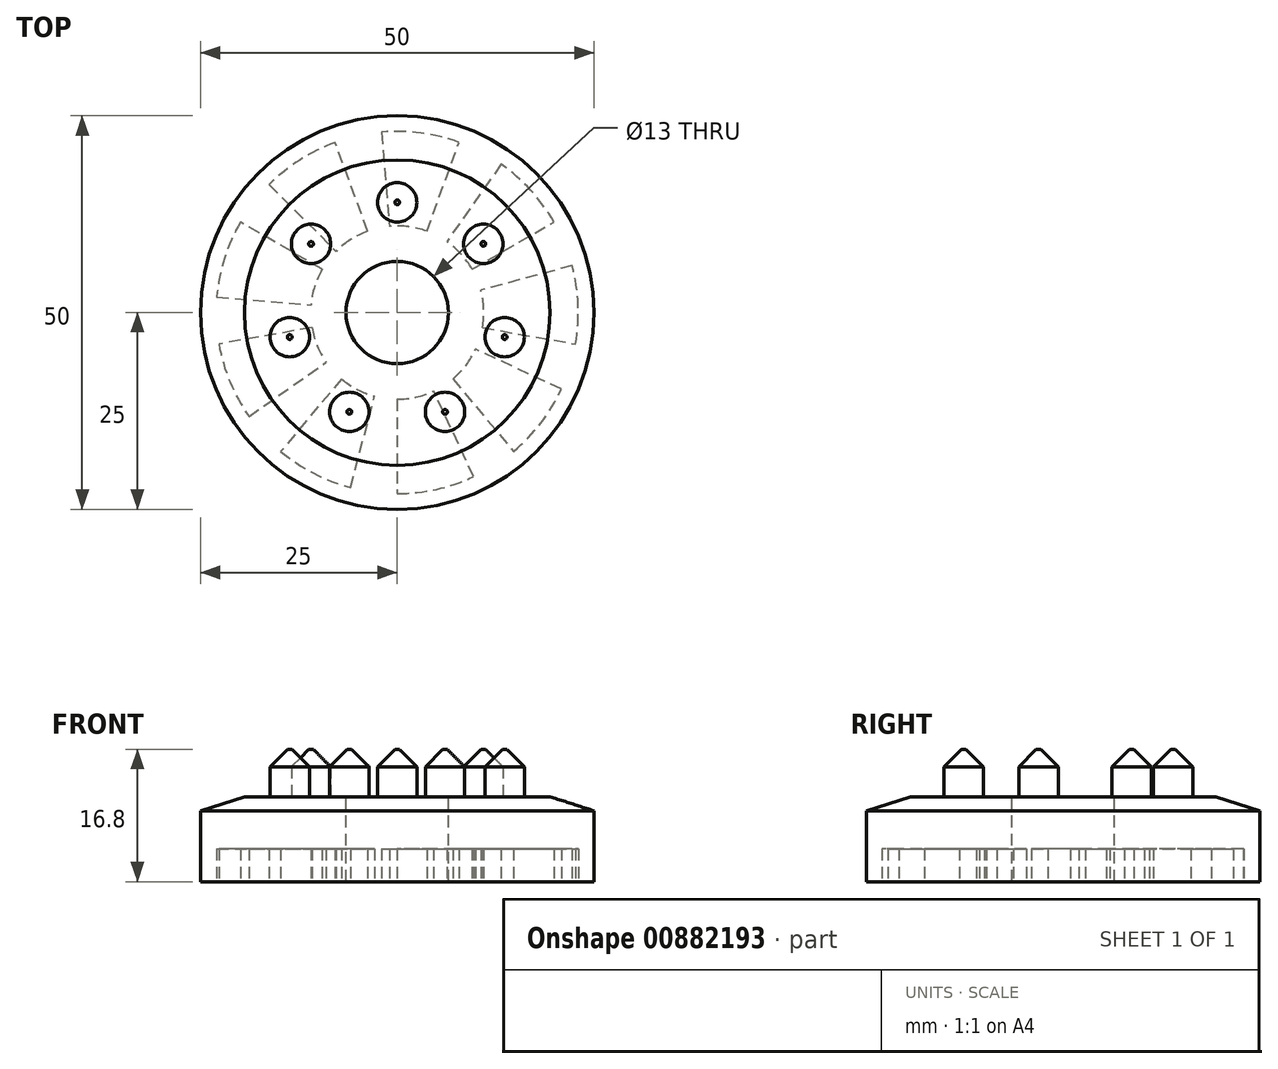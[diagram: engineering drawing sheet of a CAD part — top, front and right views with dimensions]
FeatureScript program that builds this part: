
annotation { "Feature Type Name" : "Feature", "Feature Type Description" : "" }
export const myFeature = defineFeature(function(context is Context, id is Id, definition is map)
    precondition{}
    {
        {
            var Q0;
            Q0=qCreatedBy(makeId("Top.planeOp"),FACE);
            var sketch = newSketch(context, id + "F0", { "sketchPlane" : qUnion([Q0])});
            skCircle(sketch, "E0", {"center": v(0, 0) * mm, "radius": 25 * mm});
            skSolve(sketch);
        }
        {
            var Q0;
            Q0 = qSketchRegion(id + "F0", true);
            extrude(context, id + "F1", {"entities" : qUnion([Q0]), "depth" : 10.8 * mm, "offsetDistance" : 25 * mm});
        }
        {
            var Q0;
            Q0=makeQuery(id+"F1.opExtrude","CAP_EDGE",EDGE,{"disambiguationData":[OSD([sQuery(id+"F0.wireOp",EDGE,"E0")])],"isStart":false});
            chamfer(context, id + "F2", {"entities" : qUnion([Q0]), "chamferType" : ChamferType.TWO_OFFSETS, "width1" : 5.6 * mm, "oppositeDirection" : false, "width2" : 1.8 * mm, "tangentPropagation" : true});
        }
        {
            var Q0;
            Q0=makeQuery(id+"F1.opExtrude","CAP_FACE",FACE,{"disambiguationData":[OSD([sQuery(id+"F0.wireOp",EDGE,"E0")])],"isStart":false});
            var sketch = newSketch(context, id + "F3", { "sketchPlane" : qUnion([Q0])});
            skCircle(sketch, "E1", {"center": v(0, 0) * mm, "radius": 6.5 * mm});
            skCircle(sketch, "E2", {"center": v(0, 14) * mm, "radius": 2.5 * mm});
            skCircle(sketch, "E3.1.0", {"center": v(-10.95, 8.73) * mm, "radius": 2.5 * mm});
            skCircle(sketch, "E3.2.0", {"center": v(-13.65, -3.12) * mm, "radius": 2.5 * mm});
            skCircle(sketch, "E3.3.0", {"center": v(-6.07, -12.61) * mm, "radius": 2.5 * mm});
            skCircle(sketch, "E3.4.0", {"center": v(6.07, -12.61) * mm, "radius": 2.5 * mm});
            skCircle(sketch, "E3.5.0", {"center": v(13.65, -3.12) * mm, "radius": 2.5 * mm});
            skCircle(sketch, "E3.6.0", {"center": v(10.95, 8.73) * mm, "radius": 2.5 * mm});
            skSolve(sketch);
        }
        {
            var Q0;
            Q0=makeQuery(id+"F3.imprint","IMPRINT",FACE,{"disambiguationData":[TD([[makeQuery(id+"F3.imprint","IMPRINT",EDGE,{"derivedFrom":sQuery(id+"F3.wireOp",EDGE,"E3.1.0")}),1.0]])]});
            var Q1;
            Q1=makeQuery(id+"F3.imprint","IMPRINT",FACE,{"disambiguationData":[TD([[makeQuery(id+"F3.imprint","IMPRINT",EDGE,{"derivedFrom":sQuery(id+"F3.wireOp",EDGE,"E2")}),1.0]])]});
            var Q2;
            Q2=makeQuery(id+"F3.imprint","IMPRINT",FACE,{"disambiguationData":[TD([[makeQuery(id+"F3.imprint","IMPRINT",EDGE,{"derivedFrom":sQuery(id+"F3.wireOp",EDGE,"E3.6.0")}),1.0]])]});
            var Q3;
            Q3=makeQuery(id+"F3.imprint","IMPRINT",FACE,{"disambiguationData":[TD([[makeQuery(id+"F3.imprint","IMPRINT",EDGE,{"derivedFrom":sQuery(id+"F3.wireOp",EDGE,"E3.5.0")}),1.0]])]});
            var Q4;
            Q4=makeQuery(id+"F3.imprint","IMPRINT",FACE,{"disambiguationData":[TD([[makeQuery(id+"F3.imprint","IMPRINT",EDGE,{"derivedFrom":sQuery(id+"F3.wireOp",EDGE,"E3.4.0")}),1.0]])]});
            var Q5;
            Q5=makeQuery(id+"F3.imprint","IMPRINT",FACE,{"disambiguationData":[TD([[makeQuery(id+"F3.imprint","IMPRINT",EDGE,{"derivedFrom":sQuery(id+"F3.wireOp",EDGE,"E3.3.0")}),1.0]])]});
            var Q6;
            Q6=makeQuery(id+"F3.imprint","IMPRINT",FACE,{"disambiguationData":[TD([[makeQuery(id+"F3.imprint","IMPRINT",EDGE,{"derivedFrom":sQuery(id+"F3.wireOp",EDGE,"E3.2.0")}),1.0]])]});
            extrude(context, id + "F4", {"entities" : qUnion([Q0, Q1, Q2, Q3, Q4, Q5, Q6]), "operationType" : NewBodyOperationType.ADD, "depth" : 6 * mm, "offsetDistance" : 25 * mm});
        }
        {
            var Q0;
            Q0=makeQuery(id+"F4.opExtrude","CAP_EDGE",EDGE,{"disambiguationData":[OSD([sQuery(id+"F3.wireOp",EDGE,"E2")])],"isStart":false});
            var Q1;
            Q1=makeQuery(id+"F4.opExtrude","CAP_EDGE",EDGE,{"disambiguationData":[OSD([sQuery(id+"F3.wireOp",EDGE,"E3.6.0")])],"isStart":false});
            var Q2;
            Q2=makeQuery(id+"F4.opExtrude","CAP_EDGE",EDGE,{"disambiguationData":[OSD([sQuery(id+"F3.wireOp",EDGE,"E3.5.0")])],"isStart":false});
            var Q3;
            Q3=makeQuery(id+"F4.opExtrude","CAP_EDGE",EDGE,{"disambiguationData":[OSD([sQuery(id+"F3.wireOp",EDGE,"E3.4.0")])],"isStart":false});
            var Q4;
            Q4=makeQuery(id+"F4.opExtrude","CAP_EDGE",EDGE,{"disambiguationData":[OSD([sQuery(id+"F3.wireOp",EDGE,"E3.3.0")])],"isStart":false});
            var Q5;
            Q5=makeQuery(id+"F4.opExtrude","CAP_EDGE",EDGE,{"disambiguationData":[OSD([sQuery(id+"F3.wireOp",EDGE,"E3.2.0")])],"isStart":false});
            var Q6;
            Q6=makeQuery(id+"F4.opExtrude","CAP_EDGE",EDGE,{"disambiguationData":[OSD([sQuery(id+"F3.wireOp",EDGE,"E3.1.0")])],"isStart":false});
            chamfer(context, id + "F5", {"entities" : qUnion([Q0, Q1, Q2, Q3, Q4, Q5, Q6]), "width" : 2.2 * mm, "tangentPropagation" : true});
        }
        {
            var Q0;
            Q0=makeQuery(id+"F3.imprint","IMPRINT",FACE,{"disambiguationData":[TD([[makeQuery(id+"F3.imprint","IMPRINT",EDGE,{"derivedFrom":sQuery(id+"F3.wireOp",EDGE,"E1")}),1.0]])]});
            extrude(context, id + "F6", {"entities" : qUnion([Q0]), "operationType" : NewBodyOperationType.REMOVE, "endBound" : BoundingType.THROUGH_ALL, "oppositeDirection" : true, "depth" : 25 * mm, "offsetDistance" : 25 * mm});
        }
        {
            var Q0;
            Q0=makeQuery(id+"F1.opExtrude","CAP_FACE",FACE,{"disambiguationData":[OSD([sQuery(id+"F0.wireOp",EDGE,"E0")])],"isStart":true});
            var sketch = newSketch(context, id + "F7", { "sketchPlane" : qUnion([Q0])});
            skCircle(sketch, "E4", {"center": v(0, 0) * mm, "radius": 23 * mm});
            skCircle(sketch, "E5", {"center": v(0, 0) * mm, "radius": 11 * mm});
            skLineSegment(sketch, "E6", {"start": v(9.72, 20.85) * mm, "end": v(0, 0) * mm});
            skLineSegment(sketch, "E7", {"start": v(0, 0) * mm, "end": v(0, 23) * mm});
            skLineSegment(sketch, "E8.1.0", {"start": v(0, 0) * mm, "end": v(-14.78, 17.62) * mm});
            skLineSegment(sketch, "E8.1.1", {"start": v(-5.95, 22.22) * mm, "end": v(0, 0) * mm});
            skLineSegment(sketch, "E8.2.0", {"start": v(0, 0) * mm, "end": v(-22.65, 4) * mm});
            skLineSegment(sketch, "E8.2.1", {"start": v(-18.84, 13.2) * mm, "end": v(0, 0) * mm});
            skLineSegment(sketch, "E8.3.0", {"start": v(0, 0) * mm, "end": v(-19.92, -11.5) * mm});
            skLineSegment(sketch, "E8.3.1", {"start": v(-22.91, -2) * mm, "end": v(0, 0) * mm});
            skLineSegment(sketch, "E8.4.0", {"start": v(0, 0) * mm, "end": v(-7.87, -21.61) * mm});
            skLineSegment(sketch, "E8.4.1", {"start": v(-16.26, -16.26) * mm, "end": v(0, 0) * mm});
            skLineSegment(sketch, "E8.5.0", {"start": v(0, 0) * mm, "end": v(7.87, -21.61) * mm});
            skLineSegment(sketch, "E8.5.1", {"start": v(-2, -22.91) * mm, "end": v(0, 0) * mm});
            skLineSegment(sketch, "E8.6.0", {"start": v(0, 0) * mm, "end": v(19.92, -11.5) * mm});
            skLineSegment(sketch, "E8.6.1", {"start": v(13.2, -18.84) * mm, "end": v(0, 0) * mm});
            skLineSegment(sketch, "E8.7.0", {"start": v(0, 0) * mm, "end": v(22.65, 4) * mm});
            skLineSegment(sketch, "E8.7.1", {"start": v(22.22, -5.95) * mm, "end": v(0, 0) * mm});
            skLineSegment(sketch, "E8.8.0", {"start": v(0, 0) * mm, "end": v(14.78, 17.62) * mm});
            skLineSegment(sketch, "E8.8.1", {"start": v(20.85, 9.72) * mm, "end": v(0, 0) * mm});
            skSolve(sketch);
        }
        {
            var Q0;
            {var subQ0=sQuery(id+"F7.wireOp",EDGE,"E6");var subQ1=sQuery(id+"F7.wireOp",EDGE,"E4");var subQ2=makeQuery(id+"F7.imprint","INTERSECT",VERTEX,{"derivedFrom":[subQ1,subQ0]});Q0=makeQuery(id+"F7.imprint","IMPRINT",FACE,{"disambiguationData":[TD([[makeQuery(id+"F7.imprint","IMPRINT",EDGE,{"disambiguationData":[TD([[subQ2,-1.0]])],"derivedFrom":subQ1}),1.0]])]});}
            var Q1;
            {var subQ0=sQuery(id+"F7.wireOp",EDGE,"E8.8.0");var subQ1=sQuery(id+"F7.wireOp",EDGE,"E4");var subQ2=makeQuery(id+"F7.imprint","INTERSECT",VERTEX,{"derivedFrom":[subQ1,subQ0]});Q1=makeQuery(id+"F7.imprint","IMPRINT",FACE,{"disambiguationData":[TD([[makeQuery(id+"F7.imprint","IMPRINT",EDGE,{"disambiguationData":[TD([[subQ2,1.0]])],"derivedFrom":subQ1}),1.0]])]});}
            var Q2;
            {var subQ0=sQuery(id+"F7.wireOp",EDGE,"E8.7.0");var subQ1=sQuery(id+"F7.wireOp",EDGE,"E4");var subQ2=makeQuery(id+"F7.imprint","INTERSECT",VERTEX,{"derivedFrom":[subQ1,subQ0]});Q2=makeQuery(id+"F7.imprint","IMPRINT",FACE,{"disambiguationData":[TD([[makeQuery(id+"F7.imprint","IMPRINT",EDGE,{"disambiguationData":[TD([[subQ2,1.0]])],"derivedFrom":subQ1}),1.0]])]});}
            var Q3;
            {var subQ0=sQuery(id+"F7.wireOp",EDGE,"E8.6.0");var subQ1=sQuery(id+"F7.wireOp",EDGE,"E4");var subQ2=makeQuery(id+"F7.imprint","INTERSECT",VERTEX,{"derivedFrom":[subQ1,subQ0]});Q3=makeQuery(id+"F7.imprint","IMPRINT",FACE,{"disambiguationData":[TD([[makeQuery(id+"F7.imprint","IMPRINT",EDGE,{"disambiguationData":[TD([[subQ2,1.0]])],"derivedFrom":subQ1}),1.0]])]});}
            var Q4;
            {var subQ0=sQuery(id+"F7.wireOp",EDGE,"E8.5.0");var subQ1=sQuery(id+"F7.wireOp",EDGE,"E4");var subQ2=makeQuery(id+"F7.imprint","INTERSECT",VERTEX,{"derivedFrom":[subQ1,subQ0]});Q4=makeQuery(id+"F7.imprint","IMPRINT",FACE,{"disambiguationData":[TD([[makeQuery(id+"F7.imprint","IMPRINT",EDGE,{"disambiguationData":[TD([[subQ2,1.0]])],"derivedFrom":subQ1}),1.0]])]});}
            var Q5;
            {var subQ0=sQuery(id+"F7.wireOp",EDGE,"E8.4.0");var subQ1=sQuery(id+"F7.wireOp",EDGE,"E4");var subQ2=makeQuery(id+"F7.imprint","INTERSECT",VERTEX,{"derivedFrom":[subQ1,subQ0]});Q5=makeQuery(id+"F7.imprint","IMPRINT",FACE,{"disambiguationData":[TD([[makeQuery(id+"F7.imprint","IMPRINT",EDGE,{"disambiguationData":[TD([[subQ2,1.0]])],"derivedFrom":subQ1}),1.0]])]});}
            var Q6;
            {var subQ0=sQuery(id+"F7.wireOp",EDGE,"E8.3.0");var subQ1=sQuery(id+"F7.wireOp",EDGE,"E4");var subQ2=makeQuery(id+"F7.imprint","INTERSECT",VERTEX,{"derivedFrom":[subQ1,subQ0]});Q6=makeQuery(id+"F7.imprint","IMPRINT",FACE,{"disambiguationData":[TD([[makeQuery(id+"F7.imprint","IMPRINT",EDGE,{"disambiguationData":[TD([[subQ2,1.0]])],"derivedFrom":subQ1}),1.0]])]});}
            var Q7;
            {var subQ0=sQuery(id+"F7.wireOp",EDGE,"E8.2.0");var subQ1=sQuery(id+"F7.wireOp",EDGE,"E4");var subQ2=makeQuery(id+"F7.imprint","INTERSECT",VERTEX,{"derivedFrom":[subQ1,subQ0]});Q7=makeQuery(id+"F7.imprint","IMPRINT",FACE,{"disambiguationData":[TD([[makeQuery(id+"F7.imprint","IMPRINT",EDGE,{"disambiguationData":[TD([[subQ2,1.0]])],"derivedFrom":subQ1}),1.0]])]});}
            var Q8;
            {var subQ0=sQuery(id+"F7.wireOp",EDGE,"E8.1.0");var subQ1=sQuery(id+"F7.wireOp",EDGE,"E4");var subQ2=makeQuery(id+"F7.imprint","INTERSECT",VERTEX,{"derivedFrom":[subQ1,subQ0]});Q8=makeQuery(id+"F7.imprint","IMPRINT",FACE,{"disambiguationData":[TD([[makeQuery(id+"F7.imprint","IMPRINT",EDGE,{"disambiguationData":[TD([[subQ2,1.0]])],"derivedFrom":subQ1}),1.0]])]});}
            extrude(context, id + "F8", {"entities" : qUnion([Q0, Q1, Q2, Q3, Q4, Q5, Q6, Q7, Q8]), "operationType" : NewBodyOperationType.REMOVE, "oppositeDirection" : true, "depth" : 4.2 * mm, "offsetDistance" : 25 * mm});
        }
    });
